AUTODESK INVENTOR PART (.ipt)
format: ipt  version: 2021 (Build 250183000, 183)  size: 110,080 bytes
history: native  units: mm
features: extrude x2, sketch x1
ambient origin geometry x8: Origin, YZ Plane, XZ Plane, XY Plane, X Axis, Y Axis, Z Axis, Center Point
bodies: Solid1 (feature_tree)
feature tree (3):
  sketch  "Sketch1"  dims[d0=550.0mm d1=550.0mm d2=3.0mm d3=0.0mm d4=20.0mm d5=20.0mm d6=20.0mm d7=20.0mm d8=20.0mm d9=20.0mm d10=20.0mm d11=20.0mm d12=3.1mm d13=0.0mm]
  extrude  "Extrusion1"  Depth=550.0mm
  extrude  "Extrusion2"  Depth=3.0mm TaperAngle=0.0deg
